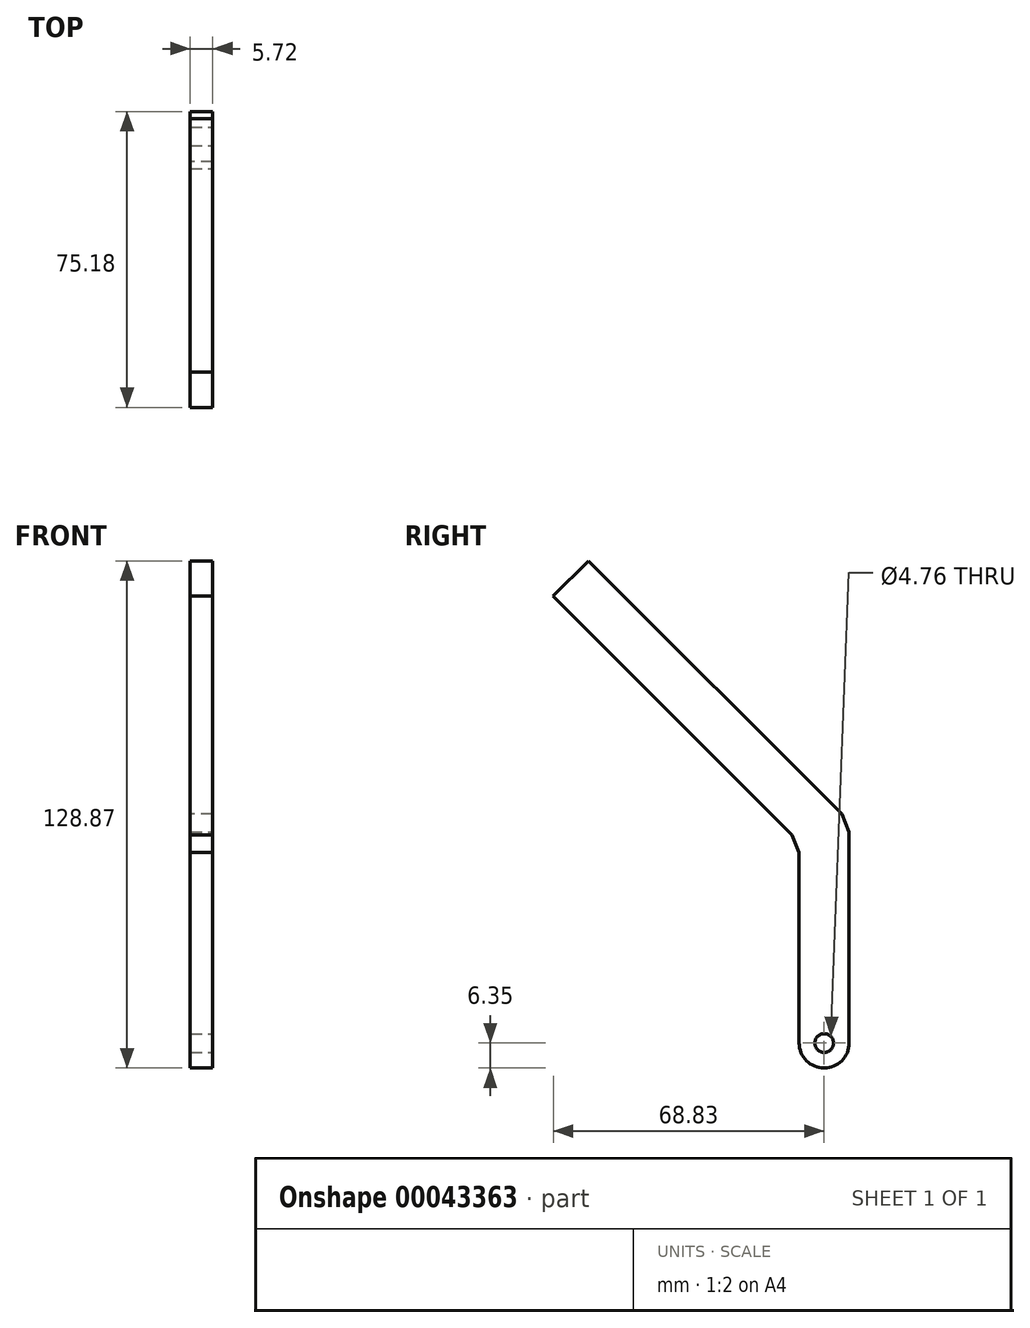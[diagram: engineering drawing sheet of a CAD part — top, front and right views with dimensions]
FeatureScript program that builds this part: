
annotation { "Feature Type Name" : "Feature", "Feature Type Description" : "" }
export const myFeature = defineFeature(function(context is Context, id is Id, definition is map)
    precondition{}
    {
        {
            var Q0;
            Q0=qCreatedBy(makeId("Right.planeOp"),FACE);
            var sketch = newSketch(context, id + "F0", { "sketchPlane" : qUnion([Q0])});
            skLineSegment(sketch, "E0", {"start": v(0, 0) * mm, "end": v(0, 53.68) * mm, "construction": true});
            skLineSegment(sketch, "E1", {"start": v(0, 53.68) * mm, "end": v(-64.34, 118.03) * mm, "construction": true});
            skLineSegment(sketch, "E2.0", {"start": v(6.35, 56.31) * mm, "end": v(-59.85, 122.52) * mm});
            skLineSegment(sketch, "E2.1", {"start": v(6.35, -6.35) * mm, "end": v(6.35, 56.31) * mm});
            skLineSegment(sketch, "E3.0", {"start": v(-6.35, 51.05) * mm, "end": v(-68.83, 113.54) * mm});
            skLineSegment(sketch, "E3.1", {"start": v(-6.35, -6.35) * mm, "end": v(-6.35, 51.05) * mm});
            skLineSegment(sketch, "E4", {"start": v(-68.83, 113.54) * mm, "end": v(-59.85, 122.52) * mm});
            skLineSegment(sketch, "E5", {"start": v(-6.35, -6.35) * mm, "end": v(6.35, -6.35) * mm});
            skSolve(sketch);
        }
        {
            var Q0;
            Q0 = qSketchRegion(id + "F0", true);
            extrude(context, id + "F1", {"entities" : qUnion([Q0]), "endBound" : BoundingType.SYMMETRIC, "depth" : 5.7 * mm});
        }
        {
            var Q0;
            Q0=makeQuery(id+"F1.opExtrude","CAP_FACE",FACE,{"disambiguationData":[OSD([sQuery(id+"F0.wireOp",EDGE,"E2.0"),sQuery(id+"F0.wireOp",EDGE,"E2.1"),sQuery(id+"F0.wireOp",EDGE,"E3.0"),sQuery(id+"F0.wireOp",EDGE,"E3.1"),sQuery(id+"F0.wireOp",EDGE,"E4"),sQuery(id+"F0.wireOp",EDGE,"E5")])],"isStart":false});
            var sketch = newSketch(context, id + "F2", { "sketchPlane" : qUnion([Q0])});
            skPoint(sketch, "E6", {"position": v(0, 0) * mm});
            skSolve(sketch);
        }
        {
            var Q0;
            Q0=sQuery(id+"F2.wireOp",VERTEX,"E6");
            var Q1;
            Q1=makeQuery(id+"F1.opExtrude","SWEPT_BODY",BODY,{"disambiguationData":[OSD([sQuery(id+"F0.wireOp",EDGE,"E2.0"),sQuery(id+"F0.wireOp",EDGE,"E2.1"),sQuery(id+"F0.wireOp",EDGE,"E3.0"),sQuery(id+"F0.wireOp",EDGE,"E3.1"),sQuery(id+"F0.wireOp",EDGE,"E4"),sQuery(id+"F0.wireOp",EDGE,"E5")])]});
            hole(context, id + "F3", {"style" : HoleStyle.SIMPLE, "holeDiameter" : 4.76 * mm, "endStyle" : HoleEndStyle.THROUGH, "locations" : qUnion([Q0]), "scope" : qUnion([Q1])});
        }
        {
            var Q0;
            Q0=makeQuery(id+"F1.opExtrude","SWEPT_EDGE",EDGE,{"disambiguationData":[OSD([sQuery(id+"F0.wireOp",EDGE,"E3.1"),sQuery(id+"F0.wireOp",EDGE,"E5")])]});
            var Q1;
            Q1=makeQuery(id+"F1.opExtrude","SWEPT_EDGE",EDGE,{"disambiguationData":[OSD([sQuery(id+"F0.wireOp",EDGE,"E2.1"),sQuery(id+"F0.wireOp",EDGE,"E5")])]});
            fillet(context, id + "F4", {"entities" : qUnion([Q0, Q1]), "radius" : 6.35 * mm, "tangentPropagation" : true, "allowEdgeOverflow" : false});
        }
        {
            var Q0;
            Q0=makeQuery(id+"F1.opExtrude","SWEPT_EDGE",EDGE,{"disambiguationData":[OSD([sQuery(id+"F0.wireOp",EDGE,"E3.0"),sQuery(id+"F0.wireOp",EDGE,"E3.1")])]});
            var Q1;
            Q1=makeQuery(id+"F1.opExtrude","SWEPT_EDGE",EDGE,{"disambiguationData":[OSD([sQuery(id+"F0.wireOp",EDGE,"E2.0"),sQuery(id+"F0.wireOp",EDGE,"E2.1")])]});
            chamfer(context, id + "F5", {"entities" : qUnion([Q0, Q1]), "width" : 6.35 * mm, "tangentPropagation" : true});
        }
    });
